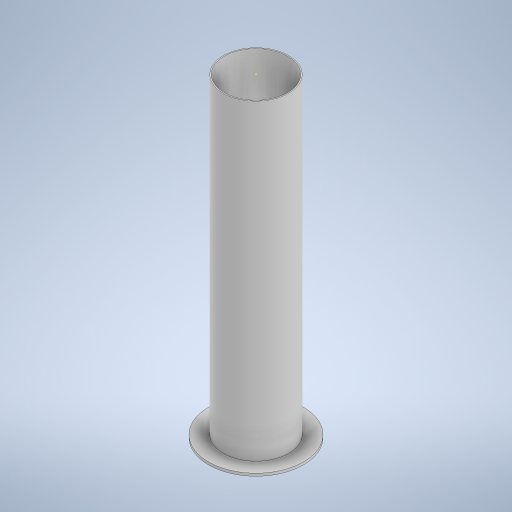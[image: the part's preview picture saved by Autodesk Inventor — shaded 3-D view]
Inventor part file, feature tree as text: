
AUTODESK INVENTOR PART (.ipt)
format: ipt  version: 2024 (Build 280153000, 153)  size: 246,784 bytes
history: native  units: mm
features: sketch x3, extrude x2, other x1
ambient origin geometry x8: Origin, YZ Plane, XZ Plane, XY Plane, X Axis, Y Axis, Z Axis, Center Point
bodies: Body1 (feature_tree)
feature tree (6):
  other  "Sólido1"
  extrude  "Extrusión1"  Depth=193.6mm
  extrude  "Extrusión2"  Depth=955.0mm
  sketch  "Boceto3"  dims[d5=8.0mm d6=0.0mm]
  sketch  "Boceto1"  dims[d0=200.0mm d1=193.6mm]
  sketch  "Boceto2"  dims[d2=955.0mm d3=0.0mm d4=290.0mm]
